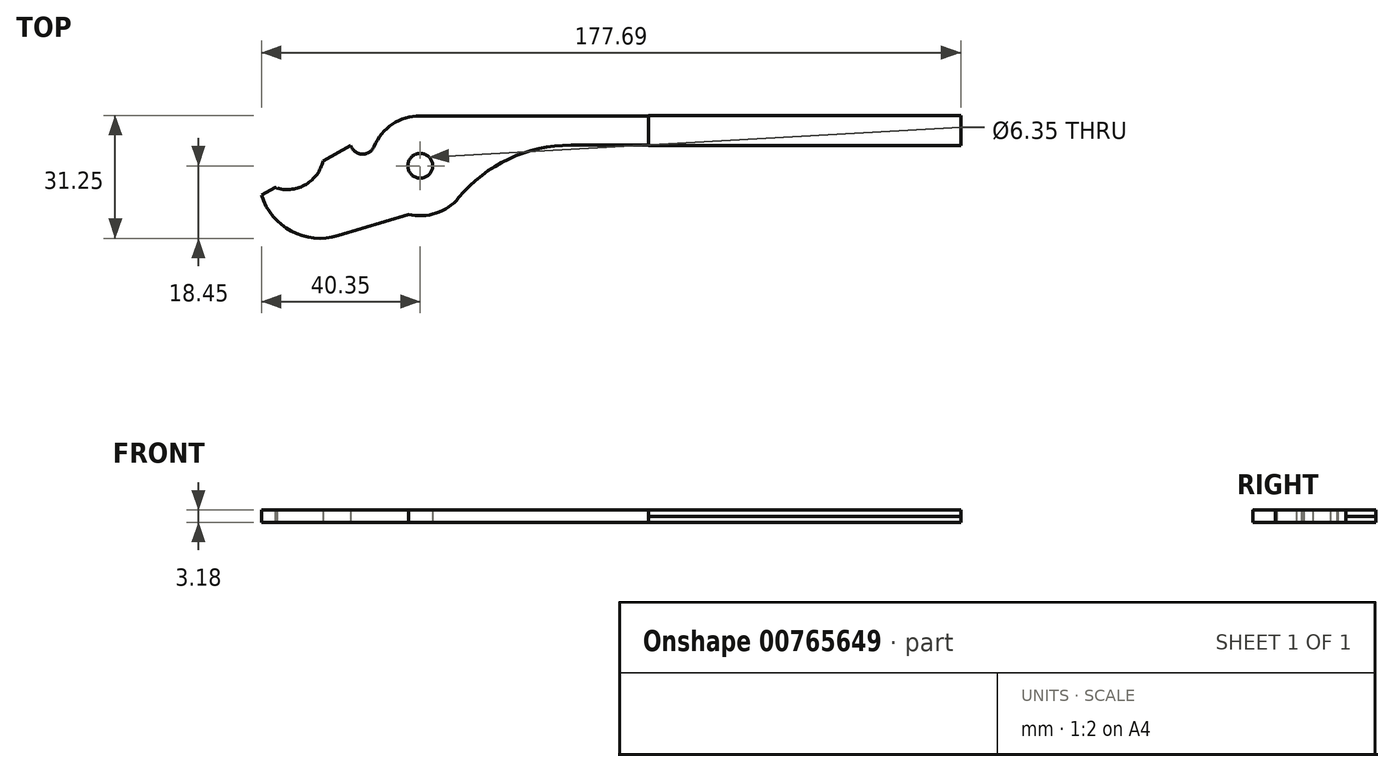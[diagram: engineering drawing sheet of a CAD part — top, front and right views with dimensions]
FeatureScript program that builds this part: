
annotation { "Feature Type Name" : "Feature", "Feature Type Description" : "" }
export const myFeature = defineFeature(function(context is Context, id is Id, definition is map)
    precondition{}
    {
        {
            var Q0;
            Q0=qCreatedBy(makeId("Top.planeOp"),FACE);
            var sketch = newSketch(context, id + "F0", { "sketchPlane" : qUnion([Q0])});
            skArc(sketch, "E0", {"start": v(-2.98, -12.34) * mm, "mid": v(4, -12.05) * mm, "end": v(9.77, -8.11) * mm});
            skArc(sketch, "E1", {"start": v(-40.35, -7.38) * mm, "mid": v(-32.75, -16.62) * mm, "end": v(-20.85, -17.78) * mm});
            skLineSegment(sketch, "E2", {"start": v(-40.35, -7.38) * mm, "end": v(-36.93, -5.5) * mm});
            skLineSegment(sketch, "E3", {"start": v(-20.85, -17.78) * mm, "end": v(-2.98, -12.34) * mm});
            skArc(sketch, "E4", {"start": v(-17.65, 5.1) * mm, "mid": v(-14.76, 2.95) * mm, "end": v(-11.72, 4.9) * mm});
            skArc(sketch, "E5", {"start": v(-36.93, -5.5) * mm, "mid": v(-29.3, -4.89) * mm, "end": v(-24.72, 1.22) * mm});
            skLineSegment(sketch, "E6.trimOffspring", {"start": v(-24.72, 1.22) * mm, "end": v(-17.65, 5.1) * mm});
            skLineSegment(sketch, "E7", {"start": v(0, 12.7) * mm, "end": v(57.96, 12.7) * mm});
            skArc(sketch, "E8", {"start": v(38.25, 5.26) * mm, "mid": v(22.52, 1.75) * mm, "end": v(9.77, -8.11) * mm});
            skLineSegment(sketch, "E9", {"start": v(35.73, 5.26) * mm, "end": v(57.96, 5.26) * mm});
            skLineSegment(sketch, "E10", {"start": v(57.96, 12.7) * mm, "end": v(57.96, 5.26) * mm});
            skArc(sketch, "E11.trimOffspring", {"start": v(0, 12.7) * mm, "mid": v(-7.04, 10.57) * mm, "end": v(-11.72, 4.9) * mm});
            skLineSegment(sketch, "E12.bottom", {"start": v(57.96, 12.8) * mm, "end": v(137.34, 12.8) * mm});
            skLineSegment(sketch, "E12.top", {"start": v(57.96, 5.16) * mm, "end": v(137.34, 5.16) * mm});
            skLineSegment(sketch, "E12.left", {"start": v(57.96, 12.8) * mm, "end": v(57.96, 5.16) * mm});
            skLineSegment(sketch, "E12.right", {"start": v(137.34, 12.8) * mm, "end": v(137.34, 5.16) * mm});
            skSolve(sketch);
        }
        {
            var Q0;
            Q0=makeQuery(id+"F0.imprint","IMPRINT",FACE,{"disambiguationData":[TD([[makeQuery(id+"F0.imprint","IMPRINT",EDGE,{"derivedFrom":sQuery(id+"F0.wireOp",EDGE,"E0")}),1.0]])]});
            var sketch = newSketch(context, id + "F1", { "sketchPlane" : qUnion([Q0])});
            skCircle(sketch, "E13", {"center": v(0, 0) * mm, "radius": 3.17 * mm});
            skSolve(sketch);
        }
        {
            var Q0;
            Q0=makeQuery(id+"F1.imprint","IMPRINT",FACE,{"disambiguationData":[TD([[makeQuery(id+"F1.imprint","IMPRINT",EDGE,{"derivedFrom":sQuery(id+"F1.wireOp",EDGE,"E13")}),-1.0]])]});
            var Q1;
            {var subQ3=sQuery(id+"F0.wireOp",EDGE,"E12.bottom");Q1=makeQuery(id+"F0.imprint","IMPRINT",FACE,{"disambiguationData":[TD([[makeQuery(id+"F0.imprint","IMPRINT",EDGE,{"derivedFrom":subQ3}),-1.0]])]});}
            extrude(context, id + "F2", {"entities" : qUnion([Q0, Q1]), "depth" : 1.59 * mm, "offsetDistance" : 25.4 * mm});
        }
        {
            var Q0;
            Q0=makeQuery(id+"F2.opExtrude","CAP_FACE",FACE,{"disambiguationData":[OSD([sQuery(id+"F0.wireOp",EDGE,"E0"),sQuery(id+"F0.wireOp",EDGE,"E1"),sQuery(id+"F0.wireOp",EDGE,"E2"),sQuery(id+"F0.wireOp",EDGE,"E3"),sQuery(id+"F0.wireOp",EDGE,"E4"),sQuery(id+"F0.wireOp",EDGE,"E5"),sQuery(id+"F0.wireOp",EDGE,"E6.trimOffspring"),sQuery(id+"F0.wireOp",EDGE,"E7"),sQuery(id+"F0.wireOp",EDGE,"E8"),sQuery(id+"F0.wireOp",EDGE,"E9"),sQuery(id+"F0.wireOp",EDGE,"E11.trimOffspring"),sQuery(id+"F0.wireOp",EDGE,"E12.left"),sQuery(id+"F1.wireOp",EDGE,"E13")])],"isStart":false});
            extrude(context, id + "F3", {"entities" : qUnion([Q0]), "operationType" : NewBodyOperationType.ADD, "depth" : 1.59 * mm, "offsetDistance" : 25.4 * mm});
        }
        {
            var Q0;
            Q0=makeQuery(id+"F2.opExtrude","CAP_FACE",FACE,{"disambiguationData":[OSD([sQuery(id+"F0.wireOp",EDGE,"E12.bottom"),sQuery(id+"F0.wireOp",EDGE,"E12.top"),sQuery(id+"F0.wireOp",EDGE,"E12.left"),sQuery(id+"F0.wireOp",EDGE,"E12.right")])],"isStart":false});
            extrude(context, id + "F4", {"entities" : qUnion([Q0]), "depth" : 1.59 * mm, "offsetDistance" : 25.4 * mm});
        }
        {
            var Q0;
            Q0=makeQuery(id+"F3.opExtrude","CAP_FACE",FACE,{"disambiguationData":[OSD([sQuery(id+"F0.wireOp",EDGE,"E0"),sQuery(id+"F0.wireOp",EDGE,"E1"),sQuery(id+"F0.wireOp",EDGE,"E2"),sQuery(id+"F0.wireOp",EDGE,"E3"),sQuery(id+"F0.wireOp",EDGE,"E4"),sQuery(id+"F0.wireOp",EDGE,"E5"),sQuery(id+"F0.wireOp",EDGE,"E6.trimOffspring"),sQuery(id+"F0.wireOp",EDGE,"E7"),sQuery(id+"F0.wireOp",EDGE,"E8"),sQuery(id+"F0.wireOp",EDGE,"E9"),sQuery(id+"F0.wireOp",EDGE,"E11.trimOffspring"),sQuery(id+"F0.wireOp",EDGE,"E12.left"),sQuery(id+"F1.wireOp",EDGE,"E13")])],"isStart":false});
            var sketch = newSketch(context, id + "F5", { "sketchPlane" : qUnion([Q0])});
            skLineSegment(sketch, "E14", {"start": v(-36.61, -5.6) * mm, "end": v(-36.61, -5.95) * mm});
            skLineSegment(sketch, "E15", {"start": v(-36.61, -5.95) * mm, "end": v(-36.28, -5.7) * mm});
            skSolve(sketch);
        }
        {
            var Q0;
            {var subQ0=sQuery(id+"F5.wireOp",EDGE,"E14");Q0=makeQuery(id+"F5.imprint","IMPRINT",FACE,{"disambiguationData":[TD([[makeQuery(id+"F5.imprint","IMPRINT",EDGE,{"derivedFrom":subQ0}),1.0]])]});}
            extrude(context, id + "F6", {"entities" : qUnion([Q0]), "operationType" : NewBodyOperationType.REMOVE, "oppositeDirection" : true, "depth" : 25.4 * mm, "offsetDistance" : 25.4 * mm});
        }
    });
